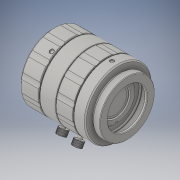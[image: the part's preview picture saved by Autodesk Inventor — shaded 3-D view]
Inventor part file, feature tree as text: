
AUTODESK INVENTOR PART (.ipt)
format: ipt  version: 2016 (Build 200138000, 138)  size: 1,580,544 bytes
history: native  units: in
note: dims shown in document units (in); Inventor stores cm internally (conversion verified against a paired STEP export)
features: revolve x1
ambient origin geometry x8: Origin, YZ Plane, XZ Plane, XY Plane, X Axis, Y Axis, Z Axis, Center Point
bodies: Solid1 (feature_tree)
feature tree (1):
  revolve  "Revolve2"  [1 undecoded]
note: 1 required parameter value undecoded (feature->parameter linkage not recoverable at this tier; creation-order binding heuristic only, values carry confidence <= 0.55)
